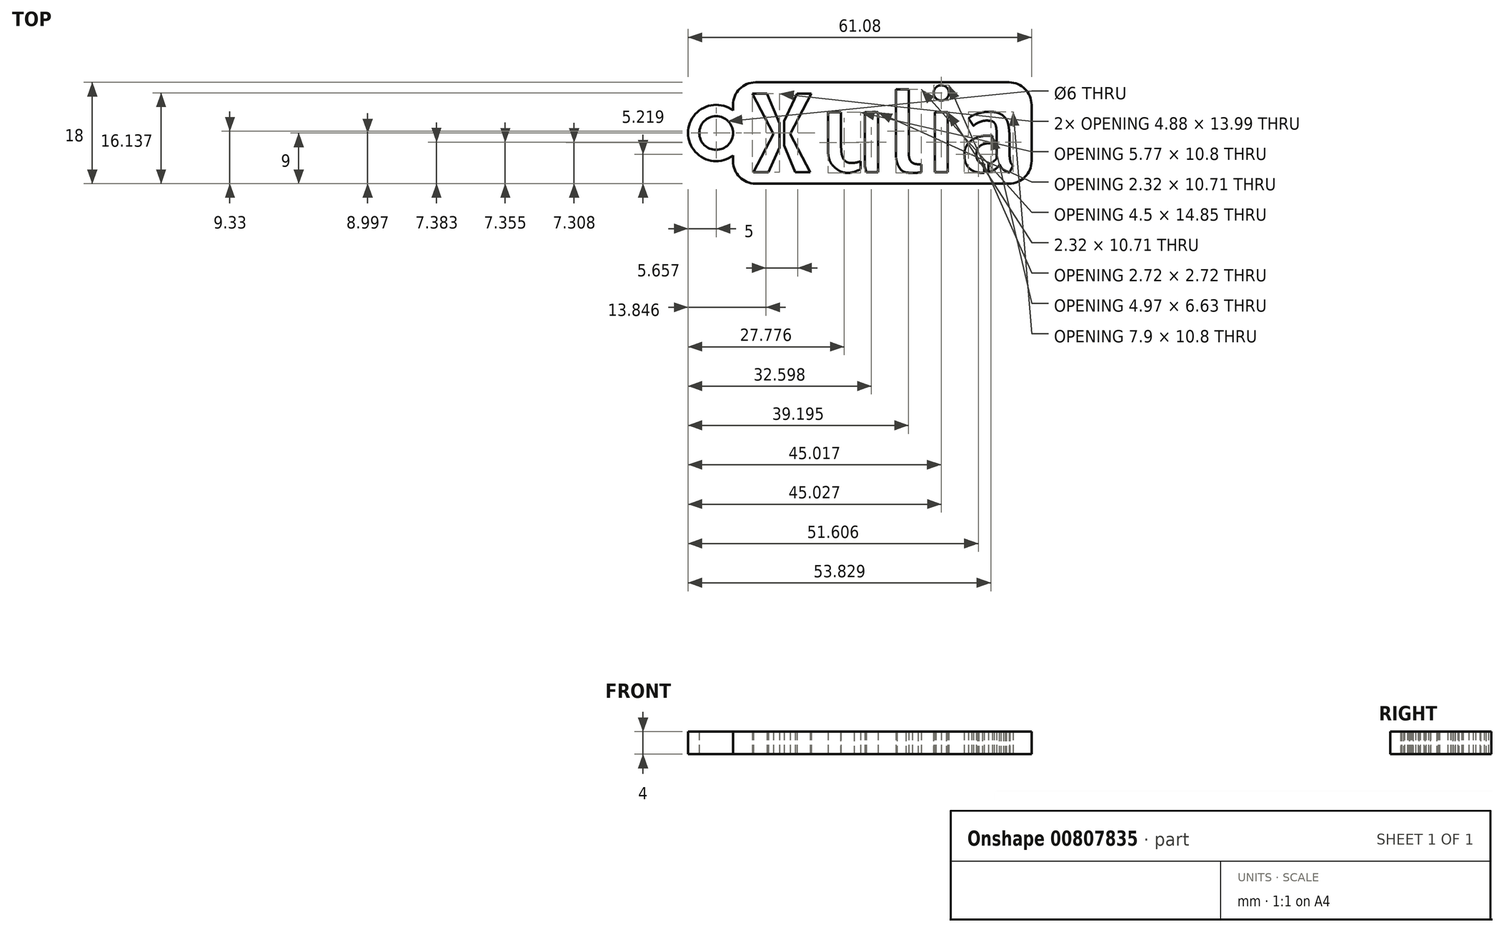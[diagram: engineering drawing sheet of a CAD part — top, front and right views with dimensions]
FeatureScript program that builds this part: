
annotation { "Feature Type Name" : "Feature", "Feature Type Description" : "" }
export const myFeature = defineFeature(function(context is Context, id is Id, definition is map)
    precondition{}
    {
        {
            var Q0;
            Q0=qCreatedBy(makeId("Top.planeOp"),FACE);
            var sketch = newSketch(context, id + "F0", { "sketchPlane" : qUnion([Q0])});
            skLineSegment(sketch, "E0.bottom", {"start": v(-2, -2) * mm, "end": v(51.08, -2) * mm});
            skLineSegment(sketch, "E0.top", {"start": v(-2, 16) * mm, "end": v(51.08, 16) * mm});
            skLineSegment(sketch, "E0.left", {"start": v(-2, -2) * mm, "end": v(-2, 3) * mm});
            skLineSegment(sketch, "E0.right", {"start": v(51.08, -2) * mm, "end": v(51.08, 16) * mm});
            skArc(sketch, "E1", {"start": v(-2, 11) * mm, "mid": v(-10, 7) * mm, "end": v(-2, 3) * mm});
            skLineSegment(sketch, "E2.trimOffspring", {"start": v(-2, 11) * mm, "end": v(-2, 16) * mm});
            skCircle(sketch, "E3", {"center": v(-5, 7) * mm, "radius": 3 * mm});
            skLineSegment(sketch, "E4", {"start": v(51.08, 7) * mm, "end": v(-10, 7) * mm, "construction": true});
            skText(sketch, "E5", { "text": "Xulia", "fontName": "AllertaStencil-Regular.ttf"});
            const initialGuessF0  = {"E5": [0, 0, 1, 0, 0.014]};
            skSetInitialGuess(sketch, initialGuessF0);
            skSolve(sketch);
        }
        {
            var Q0;
            Q0=makeQuery(id+"F0.imprint","IMPRINT",FACE,{"disambiguationData":[TD([[makeQuery(id+"F0.imprint","IMPRINT",EDGE,{"derivedFrom":sQuery(id+"F0.wireOp",EDGE,"E0.bottom")}),1.0]])]});
            extrude(context, id + "F1", {"entities" : qUnion([Q0]), "depth" : 4 * mm, "offsetDistance" : 25 * mm});
        }
        {
            var Q0;
            Q0=makeQuery(id+"F1.opExtrude","SWEPT_EDGE",EDGE,{"disambiguationData":[OSD([sQuery(id+"F0.wireOp",EDGE,"E0.bottom"),sQuery(id+"F0.wireOp",EDGE,"E0.left")])]});
            var Q1;
            Q1=makeQuery(id+"F1.opExtrude","SWEPT_EDGE",EDGE,{"disambiguationData":[OSD([sQuery(id+"F0.wireOp",EDGE,"E0.bottom"),sQuery(id+"F0.wireOp",EDGE,"E0.right")])]});
            var Q2;
            Q2=makeQuery(id+"F1.opExtrude","SWEPT_EDGE",EDGE,{"disambiguationData":[OSD([sQuery(id+"F0.wireOp",EDGE,"E0.top"),sQuery(id+"F0.wireOp",EDGE,"E0.right")])]});
            var Q3;
            Q3=makeQuery(id+"F1.opExtrude","SWEPT_EDGE",EDGE,{"disambiguationData":[OSD([sQuery(id+"F0.wireOp",EDGE,"E0.top"),sQuery(id+"F0.wireOp",EDGE,"E2.trimOffspring")])]});
            fillet(context, id + "F2", {"entities" : qUnion([Q0, Q1, Q2, Q3]), "radius" : 4 * mm, "tangentPropagation" : true, "allowEdgeOverflow" : false});
        }
    });
